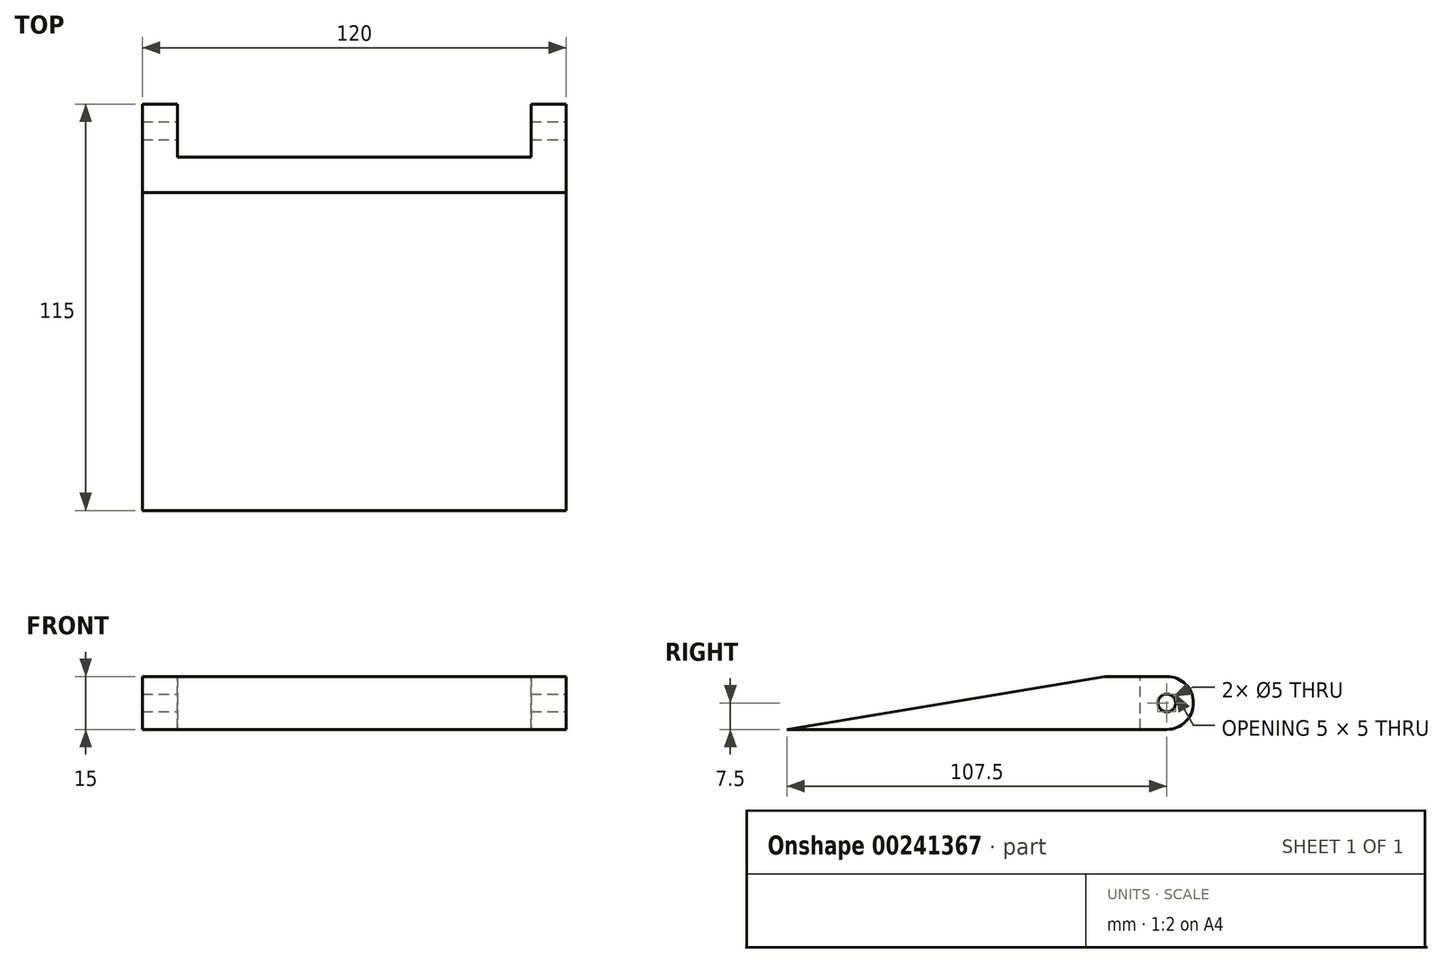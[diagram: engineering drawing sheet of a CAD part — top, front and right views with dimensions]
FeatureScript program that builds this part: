
annotation { "Feature Type Name" : "Feature", "Feature Type Description" : "" }
export const myFeature = defineFeature(function(context is Context, id is Id, definition is map)
    precondition{}
    {
        {
            var Q0;
            Q0=qCreatedBy(makeId("Top.planeOp"),FACE);
            var sketch = newSketch(context, id + "F0", { "sketchPlane" : qUnion([Q0])});
            skLineSegment(sketch, "E0.bottom", {"start": v(-60, 57.5) * mm, "end": v(60, 57.5) * mm});
            skLineSegment(sketch, "E0.top", {"start": v(-60, -57.5) * mm, "end": v(60, -57.5) * mm});
            skLineSegment(sketch, "E0.left", {"start": v(-60, 57.5) * mm, "end": v(-60, -57.5) * mm});
            skLineSegment(sketch, "E0.right", {"start": v(60, 57.5) * mm, "end": v(60, -57.5) * mm});
            skPoint(sketch, "E0.middle", {"position": v(0, 0) * mm});
            skSolve(sketch);
        }
        {
            var Q0;
            Q0 = qSketchRegion(id + "F0", true);
            extrude(context, id + "F1", {"entities" : qUnion([Q0]), "depth" : 15 * mm});
        }
        {
            var Q0;
            Q0=makeQuery(id+"F1.opExtrude","CAP_FACE",FACE,{"disambiguationData":[OSD([sQuery(id+"F0.wireOp",EDGE,"E0.bottom"),sQuery(id+"F0.wireOp",EDGE,"E0.top"),sQuery(id+"F0.wireOp",EDGE,"E0.left"),sQuery(id+"F0.wireOp",EDGE,"E0.right")])],"isStart":false});
            var sketch = newSketch(context, id + "F2", { "sketchPlane" : qUnion([Q0])});
            skLineSegment(sketch, "E1.bottom", {"start": v(-50, 57.5) * mm, "end": v(50, 57.5) * mm});
            skLineSegment(sketch, "E1.top", {"start": v(-50, 42.5) * mm, "end": v(50, 42.5) * mm});
            skLineSegment(sketch, "E1.left", {"start": v(-50, 57.5) * mm, "end": v(-50, 42.5) * mm});
            skLineSegment(sketch, "E1.right", {"start": v(50, 57.5) * mm, "end": v(50, 42.5) * mm});
            skSolve(sketch);
        }
        {
            var Q0;
            Q0 = qSketchRegion(id + "F2", true);
            extrude(context, id + "F3", {"entities" : qUnion([Q0]), "operationType" : NewBodyOperationType.REMOVE, "endBound" : BoundingType.THROUGH_ALL, "oppositeDirection" : true, "depth" : 25 * mm});
        }
        {
            var Q0;
            Q0=makeQuery(id+"F1.opExtrude","SWEPT_FACE",FACE,{"disambiguationData":[OSD([sQuery(id+"F0.wireOp",EDGE,"E0.right")])]});
            var sketch = newSketch(context, id + "F4", { "sketchPlane" : qUnion([Q0])});
            skCircle(sketch, "E2", {"center": v(50, 7.5) * mm, "radius": 2.5 * mm});
            skPoint(sketch, "E2.centerSnap0", {"position": v(57.5, 7.5) * mm});
            skSolve(sketch);
        }
        {
            var Q0;
            Q0 = qSketchRegion(id + "F4", true);
            extrude(context, id + "F5", {"entities" : qUnion([Q0]), "operationType" : NewBodyOperationType.REMOVE, "endBound" : BoundingType.THROUGH_ALL, "oppositeDirection" : true, "depth" : 25 * mm});
        }
        {
            var Q0;
            Q0=makeQuery(id+"F1.opExtrude","CAP_EDGE",EDGE,{"disambiguationData":[OSD([sQuery(id+"F0.wireOp",EDGE,"E0.top")])],"isStart":false});
            chamfer(context, id + "F6", {"entities" : qUnion([Q0]), "chamferType" : ChamferType.TWO_OFFSETS, "width1" : 90 * mm, "oppositeDirection" : false, "width2" : 15 * mm, "tangentPropagation" : true});
        }
        {
            var Q0;
            {var subQ0=sQuery(id+"F0.wireOp",EDGE,"E0.bottom");var subQ1=sQuery(id+"F0.wireOp",EDGE,"E0.right");Q0=makeQuery(id+"F3.boolean.opBoolean","SPLIT",EDGE,{"disambiguationData":[TD([makeQuery(id+"F1.opExtrude","SWEPT_FACE",FACE,{"disambiguationData":[OSD([subQ1])]})])],"derivedFrom":makeQuery(id+"F1.opExtrude","CAP_EDGE",EDGE,{"disambiguationData":[OSD([subQ0])],"isStart":false})});}
            var Q1;
            {var subQ0=sQuery(id+"F0.wireOp",EDGE,"E0.bottom");var subQ1=sQuery(id+"F0.wireOp",EDGE,"E0.right");Q1=makeQuery(id+"F3.boolean.opBoolean","SPLIT",EDGE,{"disambiguationData":[TD([makeQuery(id+"F1.opExtrude","SWEPT_FACE",FACE,{"disambiguationData":[OSD([subQ1])]})])],"derivedFrom":makeQuery(id+"F1.opExtrude","CAP_EDGE",EDGE,{"disambiguationData":[OSD([subQ0])],"isStart":true})});}
            var Q2;
            {var subQ0=sQuery(id+"F0.wireOp",EDGE,"E0.bottom");var subQ1=sQuery(id+"F0.wireOp",EDGE,"E0.left");Q2=makeQuery(id+"F3.boolean.opBoolean","SPLIT",EDGE,{"disambiguationData":[TD([makeQuery(id+"F1.opExtrude","SWEPT_FACE",FACE,{"disambiguationData":[OSD([subQ1])]})])],"derivedFrom":makeQuery(id+"F1.opExtrude","CAP_EDGE",EDGE,{"disambiguationData":[OSD([subQ0])],"isStart":true})});}
            var Q3;
            {var subQ0=sQuery(id+"F0.wireOp",EDGE,"E0.bottom");var subQ1=sQuery(id+"F0.wireOp",EDGE,"E0.left");Q3=makeQuery(id+"F3.boolean.opBoolean","SPLIT",EDGE,{"disambiguationData":[TD([makeQuery(id+"F1.opExtrude","SWEPT_FACE",FACE,{"disambiguationData":[OSD([subQ1])]})])],"derivedFrom":makeQuery(id+"F1.opExtrude","CAP_EDGE",EDGE,{"disambiguationData":[OSD([subQ0])],"isStart":false})});}
            fillet(context, id + "F7", {"entities" : qUnion([Q0, Q1, Q2, Q3]), "radius" : 7.5 * mm, "tangentPropagation" : true, "allowEdgeOverflow" : false});
        }
    });
